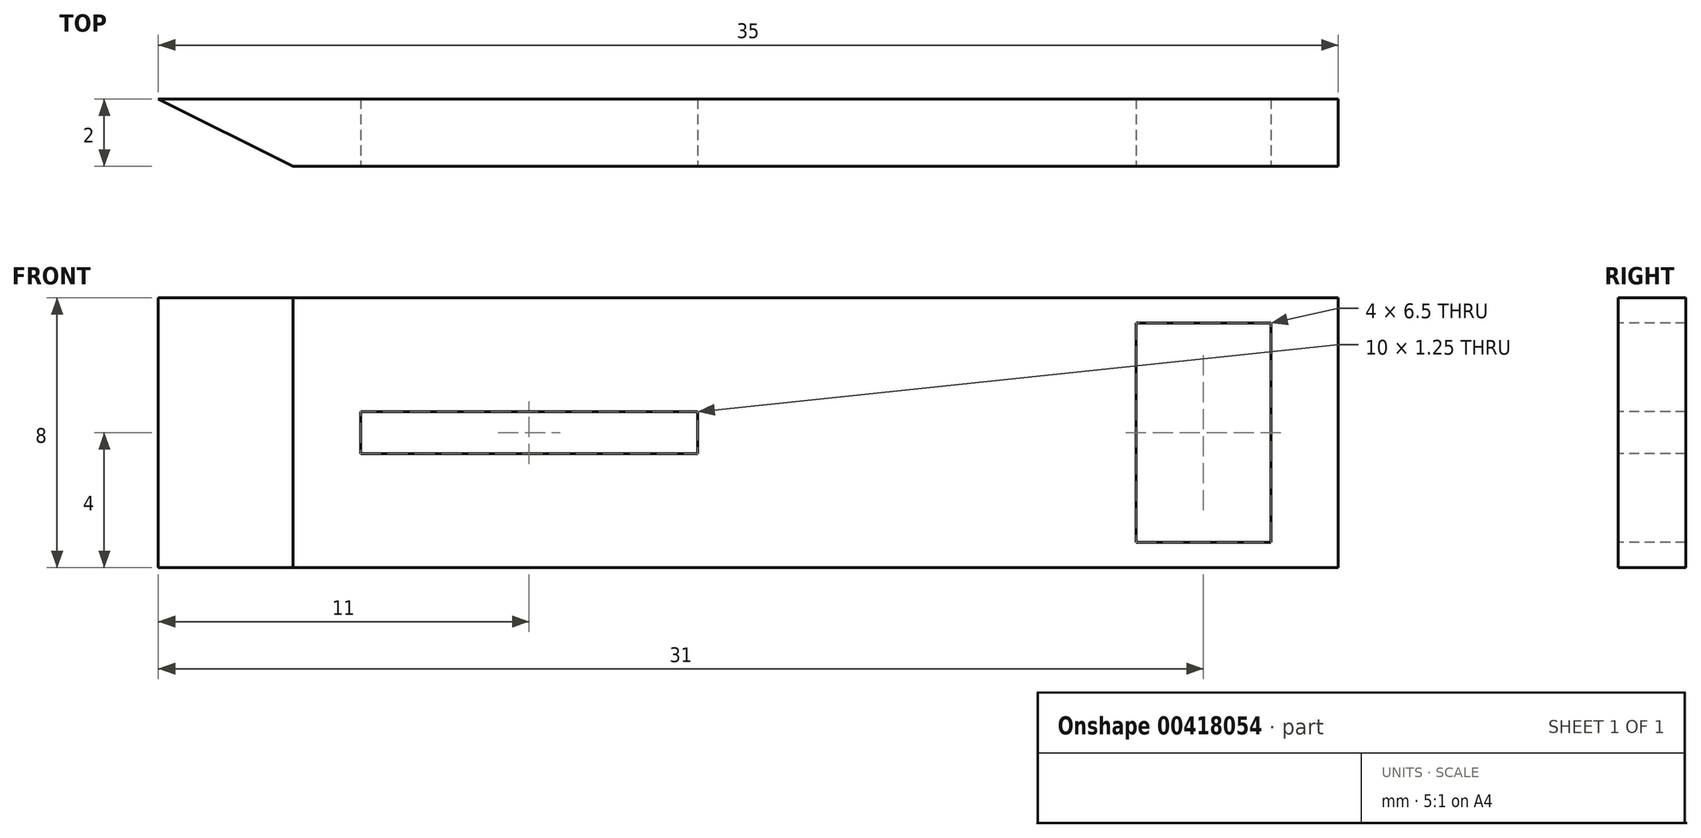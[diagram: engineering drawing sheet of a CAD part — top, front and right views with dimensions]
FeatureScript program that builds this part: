
annotation { "Feature Type Name" : "Feature", "Feature Type Description" : "" }
export const myFeature = defineFeature(function(context is Context, id is Id, definition is map)
    precondition{}
    {
        {
            var Q0;
            Q0=qCreatedBy(makeId("Front.planeOp"),FACE);
            var sketch = newSketch(context, id + "F0", { "sketchPlane" : qUnion([Q0])});
            skLineSegment(sketch, "E0.bottom", {"start": v(0, 0) * mm, "end": v(-35, 0) * mm});
            skLineSegment(sketch, "E0.top", {"start": v(0, 8) * mm, "end": v(-35, 8) * mm});
            skLineSegment(sketch, "E0.left", {"start": v(0, 0) * mm, "end": v(0, 8) * mm});
            skLineSegment(sketch, "E0.right", {"start": v(-35, 0) * mm, "end": v(-35, 8) * mm});
            skSolve(sketch);
        }
        {
            var Q0;
            Q0=makeQuery(id+"F0.imprint","IMPRINT",FACE,{"disambiguationData":[TD([[makeQuery(id+"F0.imprint","IMPRINT",EDGE,{"derivedFrom":sQuery(id+"F0.wireOp",EDGE,"E0.bottom")}),-1.0]])]});
            extrude(context, id + "F1", {"entities" : qUnion([Q0]), "depth" : 2 * mm});
        }
        {
            var Q0;
            Q0=makeQuery(id+"F1.opExtrude","CAP_EDGE",EDGE,{"disambiguationData":[OSD([sQuery(id+"F0.wireOp",EDGE,"E0.right")])],"isStart":false});
            chamfer(context, id + "F2", {"entities" : qUnion([Q0]), "chamferType" : ChamferType.TWO_OFFSETS, "width1" : 2 * mm, "oppositeDirection" : false, "width2" : 4 * mm, "tangentPropagation" : true});
        }
        {
            var Q0;
            Q0=makeQuery(id+"FNHvnfLxQbsOtxr_1.boolean.opBoolean","MERGE",FACE,{"derivedFrom":[makeQuery(id+"F1.opExtrude","CAP_FACE",FACE,{"disambiguationData":[OSD([sQuery(id+"F0.wireOp",EDGE,"E0.bottom"),sQuery(id+"F0.wireOp",EDGE,"E0.top"),sQuery(id+"F0.wireOp",EDGE,"E0.left"),sQuery(id+"F0.wireOp",EDGE,"E0.right")])],"isStart":false}),makeQuery(id+"FNHvnfLxQbsOtxr_1.opExtrude","CAP_FACE",FACE,{"disambiguationData":[OSD([sQuery(id+"FE4eZyHDEK8OG7q_1.wireOp",EDGE,"nZyC6iYC-TsEE-b7Uh-uFow-qXfyAyxrNtj2.bottom"),sQuery(id+"FE4eZyHDEK8OG7q_1.wireOp",EDGE,"nZyC6iYC-TsEE-b7Uh-uFow-qXfyAyxrNtj2.top"),sQuery(id+"FE4eZyHDEK8OG7q_1.wireOp",EDGE,"nZyC6iYC-TsEE-b7Uh-uFow-qXfyAyxrNtj2.left"),sQuery(id+"FE4eZyHDEK8OG7q_1.wireOp",EDGE,"nZyC6iYC-TsEE-b7Uh-uFow-qXfyAyxrNtj2.right")])],"isStart":false})]});
            var sketch = newSketch(context, id + "F3", { "sketchPlane" : qUnion([Q0])});
            skLineSegment(sketch, "E1.bottom", {"start": v(-2, 0.75) * mm, "end": v(-6, 0.75) * mm});
            skLineSegment(sketch, "E1.top", {"start": v(-2, 7.25) * mm, "end": v(-6, 7.25) * mm});
            skLineSegment(sketch, "E1.left", {"start": v(-2, 0.75) * mm, "end": v(-2, 7.25) * mm});
            skLineSegment(sketch, "E1.right", {"start": v(-6, 0.75) * mm, "end": v(-6, 7.25) * mm});
            skPoint(sketch, "E1.middle", {"position": v(-4, 4) * mm});
            skPoint(sketch, "E1.middle.positionSnap0", {"position": v(0, 4) * mm});
            skPoint(sketch, "E1.centerSnap0", {"position": v(0, 4) * mm});
            skSolve(sketch);
        }
        {
            var Q0;
            Q0=makeQuery(id+"F3.imprint","IMPRINT",FACE,{"disambiguationData":[TD([[makeQuery(id+"F3.imprint","IMPRINT",EDGE,{"derivedFrom":sQuery(id+"F3.wireOp",EDGE,"E1.bottom")}),-1.0]])]});
            extrude(context, id + "F4", {"entities" : qUnion([Q0]), "operationType" : NewBodyOperationType.REMOVE, "oppositeDirection" : true, "depth" : 2 * mm});
        }
        {
            var Q0;
            Q0=makeQuery(id+"FNHvnfLxQbsOtxr_1.boolean.opBoolean","MERGE",FACE,{"derivedFrom":[makeQuery(id+"F1.opExtrude","CAP_FACE",FACE,{"disambiguationData":[OSD([sQuery(id+"F0.wireOp",EDGE,"E0.bottom"),sQuery(id+"F0.wireOp",EDGE,"E0.top"),sQuery(id+"F0.wireOp",EDGE,"E0.left"),sQuery(id+"F0.wireOp",EDGE,"E0.right")])],"isStart":false}),makeQuery(id+"FNHvnfLxQbsOtxr_1.opExtrude","CAP_FACE",FACE,{"disambiguationData":[OSD([sQuery(id+"FE4eZyHDEK8OG7q_1.wireOp",EDGE,"nZyC6iYC-TsEE-b7Uh-uFow-qXfyAyxrNtj2.bottom"),sQuery(id+"FE4eZyHDEK8OG7q_1.wireOp",EDGE,"nZyC6iYC-TsEE-b7Uh-uFow-qXfyAyxrNtj2.top"),sQuery(id+"FE4eZyHDEK8OG7q_1.wireOp",EDGE,"nZyC6iYC-TsEE-b7Uh-uFow-qXfyAyxrNtj2.left"),sQuery(id+"FE4eZyHDEK8OG7q_1.wireOp",EDGE,"nZyC6iYC-TsEE-b7Uh-uFow-qXfyAyxrNtj2.right")])],"isStart":false})]});
            var sketch = newSketch(context, id + "F5", { "sketchPlane" : qUnion([Q0])});
            skPoint(sketch, "E2.centerSnap0", {"position": v(-6, 4) * mm});
            skLineSegment(sketch, "E3.bottom", {"start": v(-29, 4.63) * mm, "end": v(-19, 4.63) * mm});
            skLineSegment(sketch, "E3.top", {"start": v(-29, 3.38) * mm, "end": v(-19, 3.38) * mm});
            skLineSegment(sketch, "E3.left", {"start": v(-29, 4.63) * mm, "end": v(-29, 3.38) * mm});
            skLineSegment(sketch, "E3.right", {"start": v(-19, 4.63) * mm, "end": v(-19, 3.38) * mm});
            skPoint(sketch, "E3.middle", {"position": v(-24, 4) * mm});
            skSolve(sketch);
        }
        {
            var Q0;
            Q0=makeQuery(id+"F5.imprint","IMPRINT",FACE,{"disambiguationData":[TD([[makeQuery(id+"F5.imprint","IMPRINT",EDGE,{"derivedFrom":sQuery(id+"F5.wireOp",EDGE,"E3.bottom")}),-1.0]])]});
            extrude(context, id + "F6", {"entities" : qUnion([Q0]), "operationType" : NewBodyOperationType.REMOVE, "oppositeDirection" : true, "depth" : 2 * mm});
        }
    });
